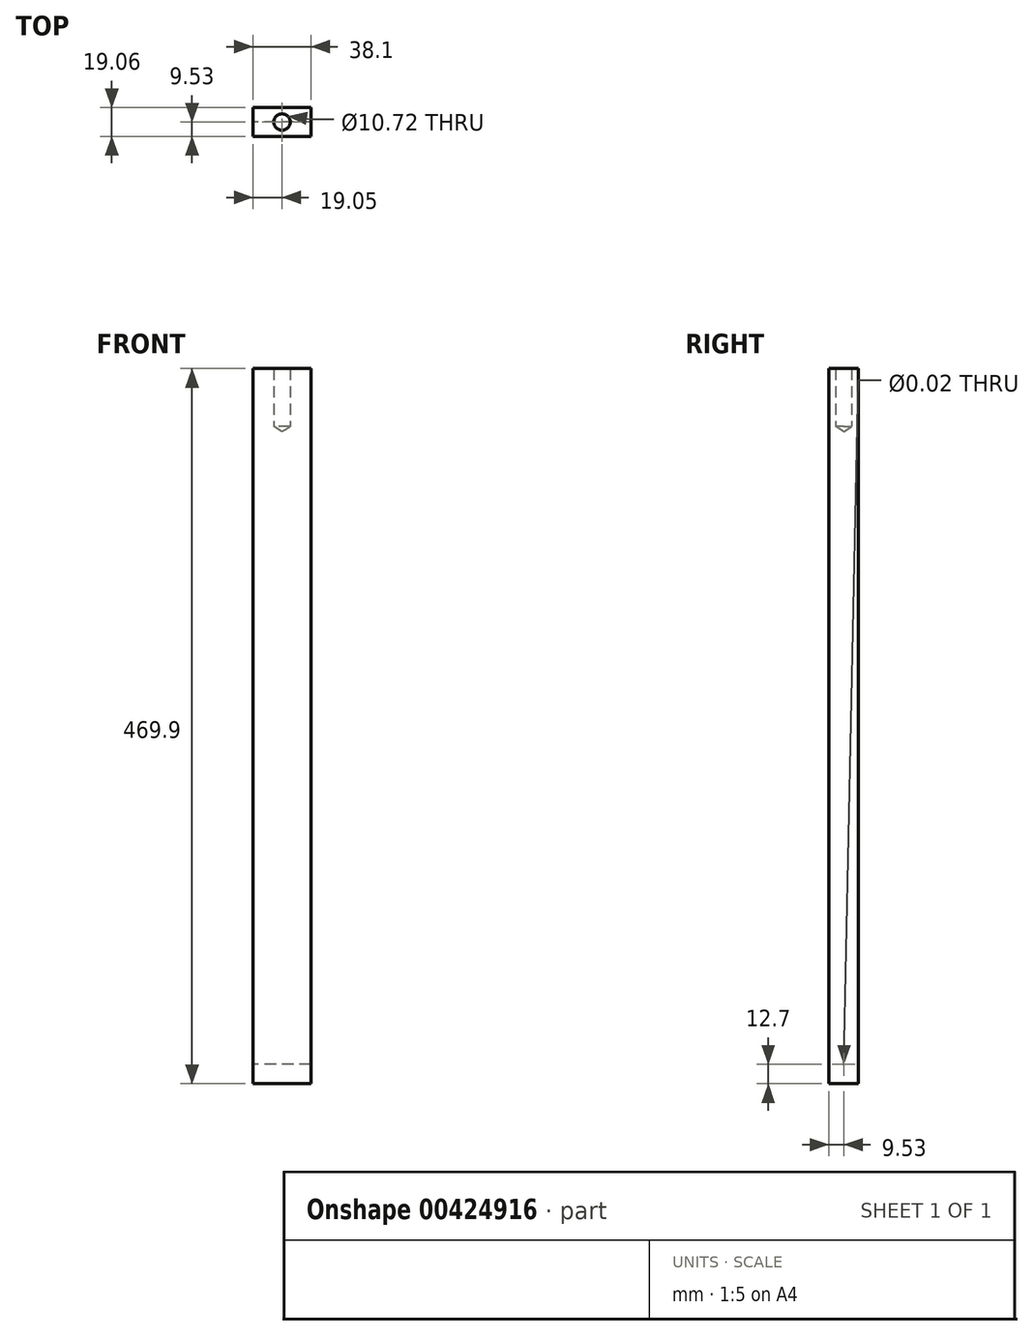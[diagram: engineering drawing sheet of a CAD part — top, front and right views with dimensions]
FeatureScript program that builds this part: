
annotation { "Feature Type Name" : "Feature", "Feature Type Description" : "" }
export const myFeature = defineFeature(function(context is Context, id is Id, definition is map)
    precondition{}
    {
        {
            var Q0;
            Q0=qCreatedBy(makeId("Top.planeOp"),FACE);
            var sketch = newSketch(context, id + "F0", { "sketchPlane" : qUnion([Q0])});
            skLineSegment(sketch, "E0.bottom", {"start": v(19.05, -9.52) * mm, "end": v(-19.05, -9.53) * mm});
            skLineSegment(sketch, "E0.top", {"start": v(19.05, 9.53) * mm, "end": v(-19.05, 9.53) * mm});
            skLineSegment(sketch, "E0.left", {"start": v(19.05, -9.52) * mm, "end": v(19.05, 9.53) * mm});
            skLineSegment(sketch, "E0.right", {"start": v(-19.05, -9.53) * mm, "end": v(-19.05, 9.53) * mm});
            skPoint(sketch, "E0.middle", {"position": v(0, 0) * mm});
            skSolve(sketch);
        }
        {
            var Q0;
            Q0=makeQuery(id+"F0.imprint","IMPRINT",FACE,{"disambiguationData":[TD([[makeQuery(id+"F0.imprint","IMPRINT",EDGE,{"derivedFrom":sQuery(id+"F0.wireOp",EDGE,"E0.bottom")}),-1.0]])]});
            extrude(context, id + "F1", {"entities" : qUnion([Q0]), "depth" : 469.9 * mm, "symmetric" : true});
        }
        {
            var Q0;
            Q0=makeQuery(id+"F1.opExtrude","SWEPT_FACE",FACE,{"disambiguationData":[OSD([sQuery(id+"F0.wireOp",EDGE,"E0.left")])]});
            var sketch = newSketch(context, id + "F2", { "sketchPlane" : qUnion([Q0])});
            skPoint(sketch, "E1", {"position": v(0, -222.25) * mm});
            skSolve(sketch);
        }
        {
            var Q0;
            Q0=sQuery(id+"F2.wireOp",VERTEX,"E1");
            var Q1;
            Q1=makeQuery(id+"F1.opExtrude","SWEPT_BODY",BODY,{"disambiguationData":[OSD([sQuery(id+"F0.wireOp",EDGE,"E0.bottom"),sQuery(id+"F0.wireOp",EDGE,"E0.top"),sQuery(id+"F0.wireOp",EDGE,"E0.left"),sQuery(id+"F0.wireOp",EDGE,"E0.right")])]});
            hole(context, id + "F3", {"style" : HoleStyle.SIMPLE, "endStyle" : HoleEndStyle.THROUGH, "standardTappedOrClearance" : lookupTablePath({ "standard" : "ANSI", "size" : "1/2 (0.5)", "type" : "Drilled" }), "standardBlindInLast" : lookupTablePath({ "standard" : "ANSI", "size" : "1/2", "type" : "Drilled" }), "holeDiameter" : 1 / 50.8 * mm, "isTappedThrough" : true, "tappedDepth" : 10.3 * mm, "tapClearance" : 3, "locations" : qUnion([Q0]), "scope" : qUnion([Q1]), "startStyle" : HoleStartStyle.SKETCH});
        }
        {
            var Q0;
            Q0=makeQuery(id+"F1.opExtrude","CAP_FACE",FACE,{"disambiguationData":[OSD([sQuery(id+"F0.wireOp",EDGE,"E0.bottom"),sQuery(id+"F0.wireOp",EDGE,"E0.top"),sQuery(id+"F0.wireOp",EDGE,"E0.left"),sQuery(id+"F0.wireOp",EDGE,"E0.right")])],"isStart":false});
            var sketch = newSketch(context, id + "F4", { "sketchPlane" : qUnion([Q0])});
            skPoint(sketch, "E2", {"position": v(0, 0) * mm});
            skSolve(sketch);
        }
        {
            var Q0;
            Q0=sQuery(id+"F4.wireOp",VERTEX,"E2");
            var Q1;
            Q1=makeQuery(id+"F1.opExtrude","SWEPT_BODY",BODY,{"disambiguationData":[OSD([sQuery(id+"F0.wireOp",EDGE,"E0.bottom"),sQuery(id+"F0.wireOp",EDGE,"E0.top"),sQuery(id+"F0.wireOp",EDGE,"E0.left"),sQuery(id+"F0.wireOp",EDGE,"E0.right")])]});
            hole(context, id + "F5", {"style" : HoleStyle.SIMPLE, "endStyle" : HoleEndStyle.BLIND, "standardTappedOrClearance" : lookupTablePath({ "standard" : "ANSI", "engagement" : "75%", "pitch" : "13 tpi", "size" : "1/2", "type" : "Tapped" }), "standardBlindInLast" : lookupTablePath({ "standard" : "ANSI", "engagement" : "75%", "pitch" : "13 tpi", "size" : "1/2", "type" : "Tapped" }), "holeDiameter" : 10.72 * mm, "showTappedDepth" : true, "holeDepth" : 38.1 * mm, "isTappedThrough" : true, "tappedDepth" : 32.24 * mm, "tapClearance" : 3, "locations" : qUnion([Q0]), "scope" : qUnion([Q1]), "majorDiameter" : 12.7 * mm, "startStyle" : HoleStartStyle.SKETCH});
        }
    });
